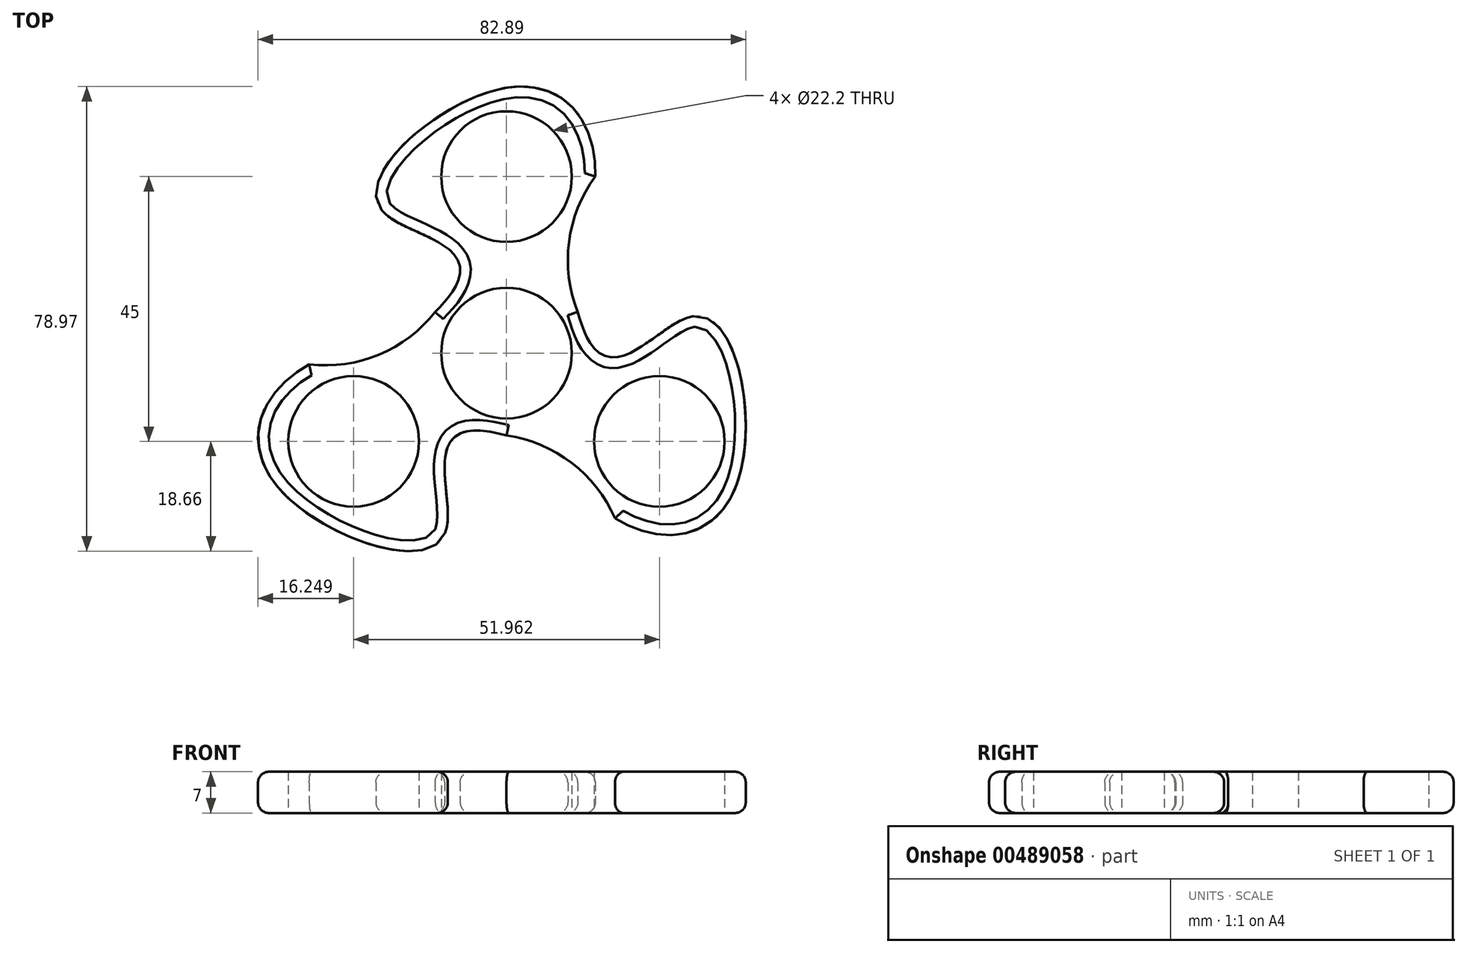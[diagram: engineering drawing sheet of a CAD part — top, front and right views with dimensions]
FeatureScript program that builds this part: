
annotation { "Feature Type Name" : "Feature", "Feature Type Description" : "" }
export const myFeature = defineFeature(function(context is Context, id is Id, definition is map)
    precondition{}
    {
        {
            var Q0;
            Q0=qCreatedBy(makeId("Top.planeOp"),FACE);
            var sketch = newSketch(context, id + "F0", { "sketchPlane" : qUnion([Q0])});
            skCircle(sketch, "E0", {"center": v(0, 0) * mm, "radius": 11.1 * mm});
            skCircle(sketch, "E1", {"center": v(0, 30) * mm, "radius": 11.1 * mm});
            skLineSegment(sketch, "E2", {"start": v(0, 30) * mm, "end": v(15.1, 30) * mm, "construction": true});
            skLineSegment(sketch, "E3", {"start": v(0, 30) * mm, "end": v(0, 45.1) * mm, "construction": true});
            skLineSegment(sketch, "E4", {"start": v(0, 0) * mm, "end": v(-12.12, 7) * mm, "construction": true});
            skLineSegment(sketch, "E5.1.0", {"start": v(0, 0) * mm, "end": v(0, -14) * mm, "construction": true});
            skLineSegment(sketch, "E5.2.0", {"start": v(0, 0) * mm, "end": v(12.12, 7) * mm, "construction": true});
            skLineSegment(sketch, "E6.1.0", {"start": v(15.1, 30) * mm, "end": v(15.29, 40.07) * mm});
            skLineSegment(sketch, "E7", {"start": v(0, 30) * mm, "end": v(-21.25, 24.3) * mm});
            skCircle(sketch, "E8.1.0", {"center": v(-25.98, -15) * mm, "radius": 11.1 * mm});
            skLineSegment(sketch, "E8.1.1", {"start": v(-25.98, -15) * mm, "end": v(-10.42, -30.56) * mm});
            skLineSegment(sketch, "E8.1.2", {"start": v(-25.98, -15) * mm, "end": v(-39.06, -22.55) * mm, "construction": true});
            skLineSegment(sketch, "E8.1.3", {"start": v(-25.98, -15) * mm, "end": v(-33.53, -1.92) * mm, "construction": true});
            skLineSegment(sketch, "E8.1.4", {"start": v(-33.53, -1.92) * mm, "end": v(-42.35, -6.8) * mm});
            skCircle(sketch, "E8.2.0", {"center": v(25.98, -15) * mm, "radius": 11.1 * mm});
            skLineSegment(sketch, "E8.2.1", {"start": v(25.98, -15) * mm, "end": v(31.67, 6.25) * mm});
            skLineSegment(sketch, "E8.2.2", {"start": v(25.98, -15) * mm, "end": v(39.06, -22.55) * mm, "construction": true});
            skLineSegment(sketch, "E8.2.3", {"start": v(25.98, -15) * mm, "end": v(18.43, -28.08) * mm, "construction": true});
            skLineSegment(sketch, "E8.2.4", {"start": v(18.43, -28.08) * mm, "end": v(27.06, -33.28) * mm});
            skFitSpline(sketch, "E9", {"points": [v(15.1, 30) * mm, v(0, 45.1) * mm, v(-21.25, 24.3) * mm, v(-12.12, 7) * mm], "startDerivative": vector(1.76, 94.8) * mm, "endDerivative": vector(-119.21, -117) * mm});
            skFitSpline(sketch, "E10", {"points": [v(-33.53, -1.92) * mm, v(-39.06, -22.55) * mm, v(-10.42, -30.56) * mm, v(0, -14) * mm], "startDerivative": vector(-82.97, -45.87) * mm, "endDerivative": vector(160.94, -44.74) * mm});
            skFitSpline(sketch, "E11", {"points": [v(18.43, -28.08) * mm, v(39.06, -22.55) * mm, v(31.67, 6.25) * mm, v(12.12, 7) * mm], "startDerivative": vector(81.21, -48.92) * mm, "endDerivative": vector(-41.72, 161.74) * mm});
            skArc(sketch, "E12", {"start": v(-33.53, -1.92) * mm, "mid": v(-21.67, -0.25) * mm, "end": v(-12.12, 7) * mm});
            skArc(sketch, "E13.1.0", {"start": v(18.43, -28.08) * mm, "mid": v(11.05, -18.64) * mm, "end": v(0, -14) * mm});
            skArc(sketch, "E13.2.0", {"start": v(15.1, 30) * mm, "mid": v(10.62, 18.89) * mm, "end": v(12.12, 7) * mm});
            skSolve(sketch);
        }
        {
            var Q0;
            Q0=makeQuery(id+"F0.imprint","IMPRINT",FACE,{"disambiguationData":[TD([[makeQuery(id+"F0.imprint","IMPRINT",EDGE,{"derivedFrom":sQuery(id+"F0.wireOp",EDGE,"E0")}),-1.0]])]});
            extrude(context, id + "F1", {"entities" : qUnion([Q0]), "endBound" : BoundingType.SYMMETRIC, "depth" : 7 * mm});
        }
        {
            var Q0;
            Q0=makeQuery(id+"F1.opExtrude","CAP_EDGE",EDGE,{"disambiguationData":[OSD([sQuery(id+"F0.wireOp",EDGE,"E9")])],"isStart":false});
            var Q1;
            Q1=makeQuery(id+"F1.opExtrude","CAP_EDGE",EDGE,{"disambiguationData":[OSD([sQuery(id+"F0.wireOp",EDGE,"E12")])],"isStart":false});
            var Q2;
            Q2=makeQuery(id+"F1.opExtrude","CAP_EDGE",EDGE,{"disambiguationData":[OSD([sQuery(id+"F0.wireOp",EDGE,"E10")])],"isStart":false});
            var Q3;
            Q3=makeQuery(id+"F1.opExtrude","CAP_EDGE",EDGE,{"disambiguationData":[OSD([sQuery(id+"F0.wireOp",EDGE,"E13.1.0")])],"isStart":false});
            var Q4;
            Q4=makeQuery(id+"F1.opExtrude","CAP_EDGE",EDGE,{"disambiguationData":[OSD([sQuery(id+"F0.wireOp",EDGE,"E11")])],"isStart":false});
            var Q5;
            Q5=makeQuery(id+"F1.opExtrude","CAP_EDGE",EDGE,{"disambiguationData":[OSD([sQuery(id+"F0.wireOp",EDGE,"E13.2.0")])],"isStart":false});
            var Q6;
            Q6=makeQuery(id+"F1.opExtrude","CAP_EDGE",EDGE,{"disambiguationData":[OSD([sQuery(id+"F0.wireOp",EDGE,"E11")])],"isStart":true});
            var Q7;
            Q7=makeQuery(id+"F1.opExtrude","CAP_EDGE",EDGE,{"disambiguationData":[OSD([sQuery(id+"F0.wireOp",EDGE,"E13.2.0")])],"isStart":true});
            var Q8;
            Q8=makeQuery(id+"F1.opExtrude","CAP_EDGE",EDGE,{"disambiguationData":[OSD([sQuery(id+"F0.wireOp",EDGE,"E9")])],"isStart":true});
            var Q9;
            Q9=makeQuery(id+"F1.opExtrude","CAP_EDGE",EDGE,{"disambiguationData":[OSD([sQuery(id+"F0.wireOp",EDGE,"E12")])],"isStart":true});
            var Q10;
            Q10=makeQuery(id+"F1.opExtrude","CAP_EDGE",EDGE,{"disambiguationData":[OSD([sQuery(id+"F0.wireOp",EDGE,"E10")])],"isStart":true});
            var Q11;
            Q11=makeQuery(id+"F1.opExtrude","CAP_EDGE",EDGE,{"disambiguationData":[OSD([sQuery(id+"F0.wireOp",EDGE,"E13.1.0")])],"isStart":true});
            fillet(context, id + "F2", {"entities" : qUnion([Q0, Q1, Q2, Q3, Q4, Q5, Q6, Q7, Q8, Q9, Q10, Q11]), "radius" : 1.8 * mm, "tangentPropagation" : true, "allowEdgeOverflow" : false});
        }
    });
